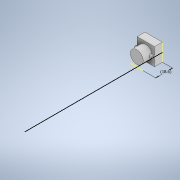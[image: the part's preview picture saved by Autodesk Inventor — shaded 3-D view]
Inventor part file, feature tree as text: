
AUTODESK INVENTOR PART (.ipt)
format: ipt  version: 2020 (Build 240168000, 168)  size: 153,088 bytes
history: native  units: in
note: dims shown in document units (in); Inventor stores cm internally (conversion verified against a paired STEP export)
features: sketch x5, extrude x3, projected_geometry x3
ambient origin geometry x8: Origin, YZ Plane, XZ Plane, XY Plane, X Axis, Y Axis, Z Axis, Center Point
bodies: Solid1 (feature_tree)
feature tree (11):
  extrude  "Extrusion1"  Depth=0.752in
  extrude  "Extrusion2"  Depth=0.4331in
  extrude  "Extrusion3"  Depth=0.1575in
  sketch  "Sketch4"  dims[d7=0.3413in d8=0.0in]
  sketch  "Sketch5"  dims[d9=0.5512in d10=0.3909in d11=0.0in d12=0.7323in]
  sketch  "Sketch1"  dims[d0=0.752in d1=0.752in]
  sketch  "Sketch2"  dims[d2=0.3413in d3=0.0in d4=0.4331in]
  projected_geometry  "Projected Loop1"
  sketch  "Sketch3"  dims[d5=0.0787in d6=0.1575in]
  projected_geometry  "Projected Loop2"
  projected_geometry  "Projected Loop3"
